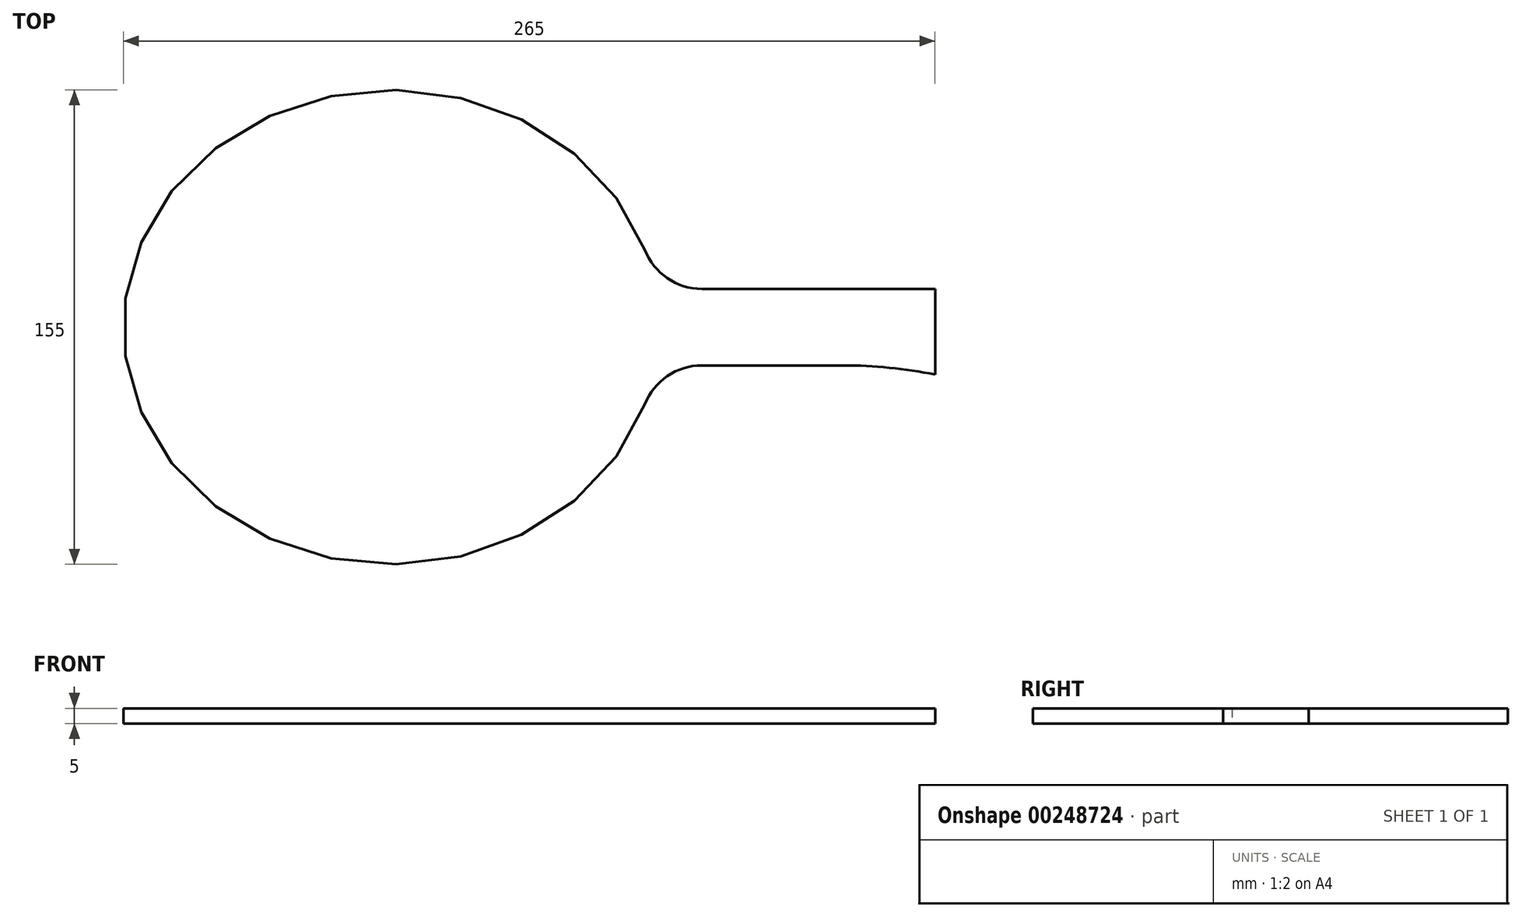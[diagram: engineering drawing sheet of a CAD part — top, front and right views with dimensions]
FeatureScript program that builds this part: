
annotation { "Feature Type Name" : "Feature", "Feature Type Description" : "" }
export const myFeature = defineFeature(function(context is Context, id is Id, definition is map)
    precondition{}
    {
        {
            var Q0;
            Q0=qCreatedBy(makeId("Top.planeOp"),FACE);
            var sketch = newSketch(context, id + "F0", { "sketchPlane" : qUnion([Q0])});
            skLineSegment(sketch, "E0", {"start": v(79.9, 0) * mm, "end": v(-95.1, 0) * mm});
            skLineSegment(sketch, "E1", {"start": v(-7.6, 0) * mm, "end": v(-7.6, 77.5) * mm});
            skLineSegment(sketch, "E2", {"start": v(-7.6, 0) * mm, "end": v(-7.6, -77.5) * mm});
            skArc(sketch, "E3", {"start": v(79.9, 0) * mm, "mid": v(-7.6, 77.5) * mm, "end": v(-95.1, 0) * mm});
            skArc(sketch, "E4", {"start": v(-95.1, 0) * mm, "mid": v(-7.6, -77.5) * mm, "end": v(79.9, 0) * mm});
            skEllipticalArc(sketch, "E5", {});
            skLineSegment(sketch, "E6.bottom", {"start": v(-379.35, -57.25) * mm, "end": v(-269.35, -57.25) * mm});
            skLineSegment(sketch, "E6.top", {"start": v(-379.35, -82.25) * mm, "end": v(-269.35, -82.25) * mm});
            skLineSegment(sketch, "E6.left", {"start": v(-379.35, -57.25) * mm, "end": v(-379.35, -82.25) * mm});
            skLineSegment(sketch, "E6.right", {"start": v(-269.35, -57.25) * mm, "end": v(-269.35, -82.25) * mm});
            skLineSegment(sketch, "E7", {"start": v(-379.35, -57.25) * mm, "end": v(-345.48, -57.25) * mm});
            skLineSegment(sketch, "E8", {"start": v(-269.35, -57.25) * mm, "end": v(-269.35, -54.25) * mm});
            skLineSegment(sketch, "E9", {"start": v(-269.35, -54.25) * mm, "end": v(-269.35, -82.25) * mm});
            skLineSegment(sketch, "E10", {"start": v(-269.35, -85.25) * mm, "end": v(-269.35, -82.25) * mm});
            skLineSegment(sketch, "E11", {"start": v(-269.35, -57.25) * mm, "end": v(-299.35, -57.25) * mm});
            skLineSegment(sketch, "E12", {"start": v(-299.35, -57.25) * mm, "end": v(-269.35, -57.25) * mm});
            skLineSegment(sketch, "E13", {"start": v(-269.35, -82.25) * mm, "end": v(-299.35, -82.25) * mm});
            skLineSegment(sketch, "E14", {"start": v(-299.35, -82.25) * mm, "end": v(-269.35, -82.25) * mm});
            skArc(sketch, "E15", {"start": v(-269.35, -85.25) * mm, "mid": v(-284.27, -83) * mm, "end": v(-299.35, -82.25) * mm});
            skArc(sketch, "E16", {"start": v(-299.35, -57.25) * mm, "mid": v(-284.27, -56.5) * mm, "end": v(-269.35, -54.25) * mm});
            skArc(sketch, "E17", {"start": v(-364.12, -44.5) * mm, "mid": v(-356.77, -53.76) * mm, "end": v(-345.48, -57.25) * mm});
            skArc(sketch, "E18", {"start": v(-345.48, -82.25) * mm, "mid": v(-356.77, -85.75) * mm, "end": v(-364.12, -95) * mm});
            const initialGuessF0  = {"E5": [-0.44684834718704225, -0.06975328266620638, 1, 0, 0.0875, 0.0775, 0.33184386120446935, 5.951341445975113]};
            skSetInitialGuess(sketch, initialGuessF0);
            skSolve(sketch);
        }
        {
            var Q0;
            Q0=makeQuery(id+"F0.imprint","IMPRINT",FACE,{"disambiguationData":[TD([[makeQuery(id+"F0.imprint","IMPRINT",EDGE,{"derivedFrom":sQuery(id+"F0.wireOp",EDGE,"E5")}),1.0]])]});
            var Q1;
            Q1=makeQuery(id+"F0.imprint","IMPRINT",FACE,{"disambiguationData":[TD([[makeQuery(id+"F0.imprint","IMPRINT",EDGE,{"derivedFrom":sQuery(id+"F0.wireOp",EDGE,"E6.bottom")}),-1.0]])]});
            var Q2;
            {var subQ2=sQuery(id+"F0.wireOp",EDGE,"E12");Q2=makeQuery(id+"F0.imprint","IMPRINT",FACE,{"disambiguationData":[TD([[makeQuery(id+"F0.imprint","IMPRINT",EDGE,{"derivedFrom":subQ2}),1.0]])]});}
            var Q3;
            Q3=makeQuery(id+"F0.imprint","IMPRINT",FACE,{"disambiguationData":[TD([[makeQuery(id+"F0.imprint","IMPRINT",EDGE,{"derivedFrom":sQuery(id+"F0.wireOp",EDGE,"E10")}),1.0]])]});
            extrude(context, id + "F1", {"entities" : qUnion([Q0, Q1, Q2, Q3]), "depth" : 5 * mm, "offsetDistance" : 25 * mm});
        }
    });
